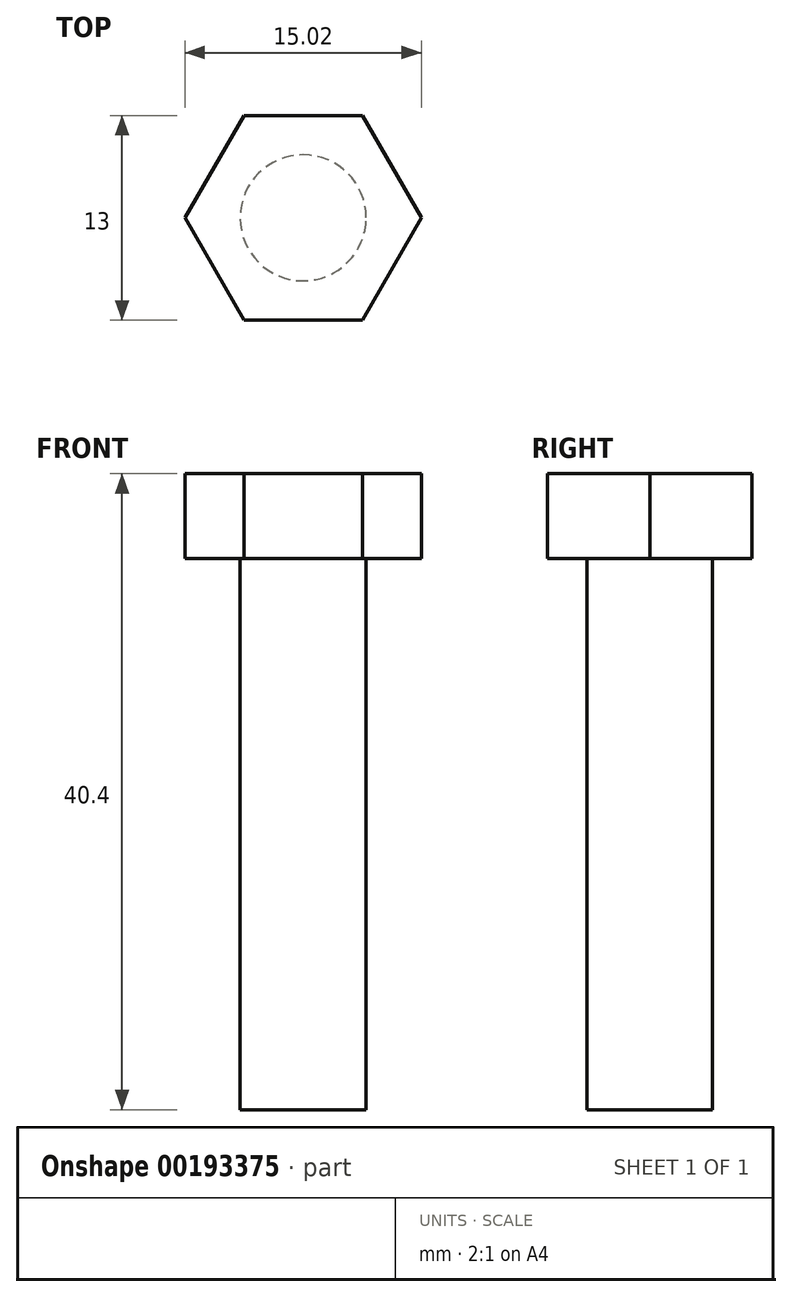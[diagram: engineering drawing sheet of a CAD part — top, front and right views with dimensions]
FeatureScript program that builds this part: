
annotation { "Feature Type Name" : "Feature", "Feature Type Description" : "" }
export const myFeature = defineFeature(function(context is Context, id is Id, definition is map)
    precondition{}
    {
        {
            var Q0;
            Q0=qCreatedBy(makeId("Top.planeOp"),FACE);
            var sketch = newSketch(context, id + "F0", { "sketchPlane" : qUnion([Q0])});
            skCircle(sketch, "E0", {"center": v(0, 0) * mm, "radius": 4 * mm});
            skSolve(sketch);
        }
        {
            var Q0;
            Q0=qSketchRegion(id+"F0",true);
            extrude(context, id + "F1", {"entities" : qUnion([Q0]), "depth" : 35 * mm, "offsetDistance" : 25 * mm});
        }
        {
            var Q0;
            Q0=makeQuery(id+"F1.opExtrude","CAP_FACE",FACE,{"disambiguationData":[OSD([sQuery(id+"F0.wireOp",EDGE,"E0")])],"isStart":false});
            var sketch = newSketch(context, id + "F2", { "sketchPlane" : qUnion([Q0])});
            skCircle(sketch, "E1.cCircle", {"center": v(0, 0) * mm, "radius": 6.5 * mm, "construction": true});
            skLineSegment(sketch, "E1.0", {"start": v(-3.75, 6.5) * mm, "end": v(3.75, 6.5) * mm});
            skLineSegment(sketch, "E1.1", {"start": v(3.75, 6.5) * mm, "end": v(7.5, 0) * mm});
            skLineSegment(sketch, "E1.2", {"start": v(7.5, 0) * mm, "end": v(3.75, -6.5) * mm});
            skLineSegment(sketch, "E1.3", {"start": v(3.75, -6.5) * mm, "end": v(-3.75, -6.5) * mm});
            skLineSegment(sketch, "E1.4", {"start": v(-3.75, -6.5) * mm, "end": v(-7.5, 0) * mm});
            skLineSegment(sketch, "E1.5", {"start": v(-7.5, 0) * mm, "end": v(-3.75, 6.5) * mm});
            skPoint(sketch, "E1.0.midPoint", {"position": v(0, 6.5) * mm});
            skSolve(sketch);
        }
        {
            var Q0;
            Q0=qSketchRegion(id+"F2",true);
            extrude(context, id + "F3", {"entities" : qUnion([Q0]), "operationType" : NewBodyOperationType.ADD, "depth" : 5.4 * mm, "offsetDistance" : 25 * mm});
        }
    });
